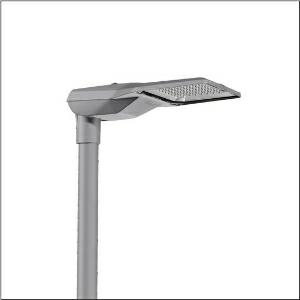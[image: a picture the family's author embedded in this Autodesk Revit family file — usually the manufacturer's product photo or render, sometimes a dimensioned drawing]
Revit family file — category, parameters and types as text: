
# Revit family: streetlight_sl_21_midi___pc-r_5xe3g33s08mb_c3de
name_source: partatom
category: Lighting Fixtures
units: mm (PartAtom-declared; Revit-internal decimal feet)

## family parameters
Cut with Voids When Loaded = No
Host = Face
Light Source = No
Part Type = Normal
Room Calculation Point = No
Round Connector Dimension = Use Diameter
Shared = No

## types (1)
- --- (1 x LED, 17390 lm, 136 W, 3000K)
    Apparent Load = 136 VA
    CIE Flux Codes = 38 78 98 100 100
    Color Rendering = 70
    Color Temperature = 3000K
    Default Elevation = 1800 mm
    Description = Streetlight SL 21 midi, mast luminaire, primary light control with lens, of PMMA, primary optical cover: cover, of toughened safety glass, transparent, light distribution: PC-R, light emission: direct distribution, primary light characteristic: asymmetric, right, installation type: side-entry, post-top, LED, High Power LED, rated luminous flux: 17.390lm, luminous efficacy: 128lm/W, light colour: 730, colour temperature: 3000K, control gear: D4i, control: overheat protection, constant luminous flux control, time-dependent luminous flux control, flexible luminous flux parameterisation, pre-setting: logarithmic dimming characteristic, mains connection: 230..240V, AC, 50/60Hz, start of lifetime: 136W, end of service life: 142W, reduction: 61W, luminaire housing, of diecast aluminium, powder-coated, SITECO metallic grey (DB 702S), corrosivity category C5 high according to DIN EN ISO 12944, please order mast flange separately, inclination adjustable: 0°, 5°, 10°, 15°, sealing non-destructively replaceable, multi-level sealing system, length: 644mm, width: 335mm, height: 110mm, mast flange for spigot size: 42mm (side-entry): 5XC10008XM4, 60/48mm (side-entry/post-top): 5XC10108XM2, 76/60mm (side-entry/post-top): 5XC10108XM1, mounting height: 4..8m, Smart Interface above, protection rating (complete): IP66, insulation class (complete): insulation class II (safety insulation), certification: CE, ENEC, ENEC+, VDE, impact resistance: IK10, permissible operating ambient temperature for outdoor applications: -40..+50°C, standard-compliant lighting for roads and squares, packaging unit: 1 piece

Light Distribution: PC-R
    Height = 111 mm
    Lamp = 1 x LED
    Lamp Light Flux = 17390 lm
    Lamp Power = 136 W
    Lamp count = 1
    Length = 644 mm
    Luminous efficacy = 128 lm/W
    Manufacturer = Siteco
    ModVariant = No
    Model = 5XE3G33S08MB
    Number of Poles = 1
    OnlyDefault = Yes
    Power Factor = 1
    Product Name = Streetlight SL 21 midi | PC-R
    Product group = mast luminaire | pylon top
    ProductGroupID = 6100
    Protection Class = Protection class II
    Protection Degree = IP 66
    RLX_Detail_Level = 1
    RLX_Emergency_Light_Flux = 0 lm
    RLX_Emergency_Type = 0
    RLX_Emergency_Type_DB = No
    RlxData = <blob elided: 29401 chars, md5=5462903d>
    Socket = socket
    Standby Power = 0 W
    System Light Flux = 17390 lm
    System Power = 136 W
    Type Comments = factory setting: luminous flux: 100 % | dim-lin: 254 | 695 mA
    Type Image = l_1004302.jpg
    URL = http://relux.com
    VarID = @adj_071851
    Voltage = 0 V
    Weight = 0.00 kg
    Width = 336 mm

## geometry (parser evidence)
native form markers: Blend x4, Sweep x10
no freeform markers — native parametric forms only
